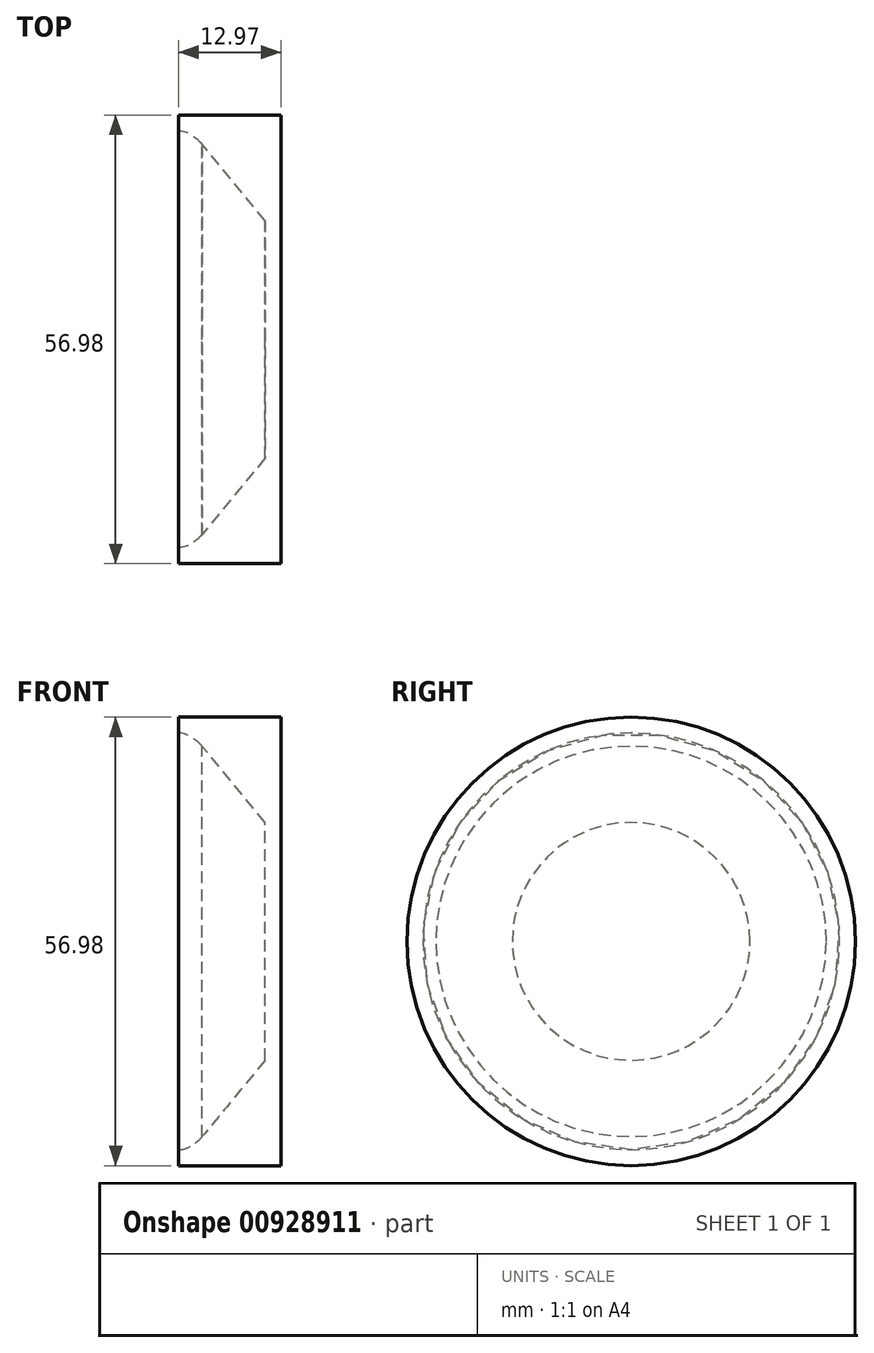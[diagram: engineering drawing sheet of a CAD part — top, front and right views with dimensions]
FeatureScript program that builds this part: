
annotation { "Feature Type Name" : "Feature", "Feature Type Description" : "" }
export const myFeature = defineFeature(function(context is Context, id is Id, definition is map)
    precondition{}
    {
        {
            var Q0;
            Q0=qCreatedBy(makeId("Front.planeOp"),FACE);
            var sketch = newSketch(context, id + "F0", { "sketchPlane" : qUnion([Q0])});
            skLineSegment(sketch, "E0", {"start": v(-8, 24.79) * mm, "end": v(0, 15.1) * mm});
            skLineSegment(sketch, "E1", {"start": v(0, 15.1) * mm, "end": v(0, 0) * mm});
            skLineSegment(sketch, "E2", {"start": v(-10.97, 26.46) * mm, "end": v(-10.97, 28.5) * mm});
            skLineSegment(sketch, "E3", {"start": v(-10.97, 28.5) * mm, "end": v(0, 28.5) * mm});
            skLineSegment(sketch, "E4", {"start": v(0, 28.5) * mm, "end": v(2, 28.5) * mm});
            skLineSegment(sketch, "E5", {"start": v(2, 28.5) * mm, "end": v(2, 0) * mm});
            skLineSegment(sketch, "E6", {"start": v(2, 0) * mm, "end": v(0, 0) * mm});
            skFitSpline(sketch, "E7.trimOffspring", {"points": [v(-14.03, 25.48) * mm, v(-10.97, 26.46) * mm, v(-9.36, 25.94) * mm, v(-8.23, 25.07) * mm, v(-8, 24.79) * mm], "startDerivative": vector(6.57, 4.44) * mm, "endDerivative": vector(1.73, -2.25) * mm});
            skSolve(sketch);
        }
        {
            var Q0;
            Q0=makeQuery(id+"F0.imprint","IMPRINT",FACE,{"disambiguationData":[TD([[makeQuery(id+"F0.imprint","IMPRINT",EDGE,{"derivedFrom":sQuery(id+"F0.wireOp",EDGE,"E0")}),1.0]])]});
            var Q1;
            Q1=sQuery(id+"F0.wireOp",EDGE,"E6");
            revolve(context, id + "F1", {"surfaceOperationType" : NewSurfaceOperationType.NEW, "entities" : qUnion([Q0]), "axis" : qUnion([Q1]), "revolveType" : RevolveType.FULL});
        }
    });
